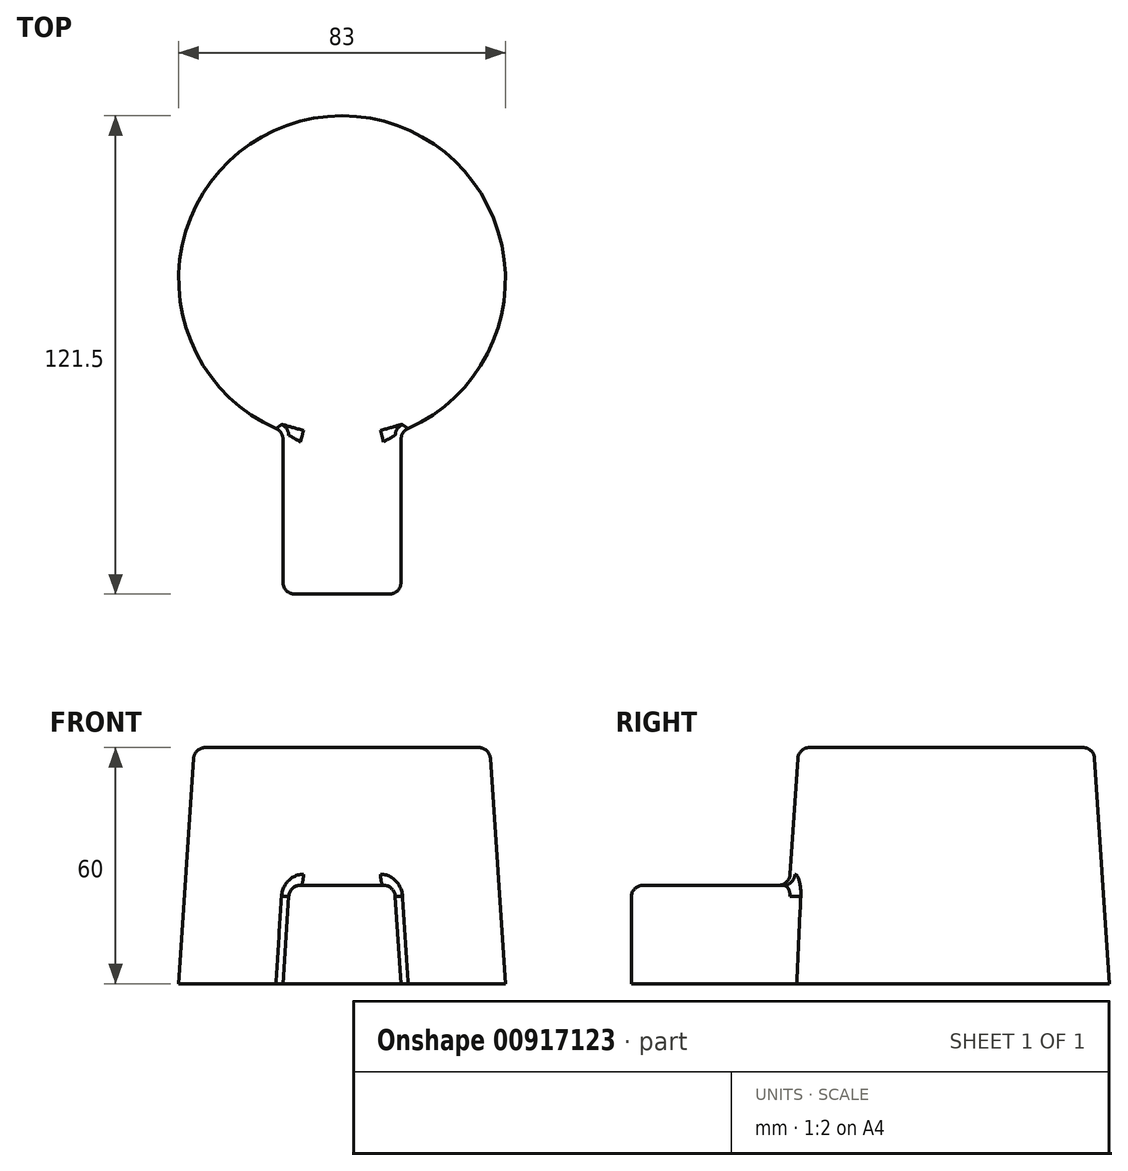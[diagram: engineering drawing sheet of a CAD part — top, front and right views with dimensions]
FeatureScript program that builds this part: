
annotation { "Feature Type Name" : "Feature", "Feature Type Description" : "" }
export const myFeature = defineFeature(function(context is Context, id is Id, definition is map)
    precondition{}
    {
        {
            var Q0;
            Q0=qCreatedBy(makeId("Top.planeOp"),FACE);
            var sketch = newSketch(context, id + "F0", { "sketchPlane" : qUnion([Q0])});
            skCircle(sketch, "E0", {"center": v(0, 0) * mm, "radius": 41.5 * mm});
            skSolve(sketch);
        }
        {
            var Q0;
            Q0 = qSketchRegion(id + "F0", true);
            extrude(context, id + "F1", {"entities" : qUnion([Q0]), "depth" : 60 * mm, "offsetDistance" : 25 * mm, "hasDraft" : true, "draftAngle" : 3.8 * degree, "draftPullDirection" : true});
        }
        {
            var Q0;
            Q0=qCreatedBy(makeId("Front.planeOp"),FACE);
            var sketch = newSketch(context, id + "F2", { "sketchPlane" : qUnion([Q0])});
            skLineSegment(sketch, "E1", {"start": v(-15, 0) * mm, "end": v(15, 0) * mm});
            skLineSegment(sketch, "E2", {"start": v(15, 0) * mm, "end": v(13.34, 25) * mm});
            skLineSegment(sketch, "E3", {"start": v(13.34, 25) * mm, "end": v(-13.34, 25) * mm});
            skLineSegment(sketch, "E4", {"start": v(-13.34, 25) * mm, "end": v(-15, 0) * mm});
            skLineSegment(sketch, "E5", {"start": v(0, 0) * mm, "end": v(0, 25) * mm, "construction": true});
            skSolve(sketch);
        }
        {
            var Q0;
            Q0 = qSketchRegion(id + "F2", true);
            extrude(context, id + "F3", {"entities" : qUnion([Q0]), "operationType" : NewBodyOperationType.ADD, "depth" : 80 * mm, "offsetDistance" : 25 * mm});
        }
        {
            var Q0;
            Q0=makeQuery(id+"F3.boolean.opBoolean","INTERSECT",EDGE,{"derivedFrom":[makeQuery(id+"F1.opExtrude","SWEPT_FACE",FACE,{"disambiguationData":[OSD([sQuery(id+"F0.wireOp",EDGE,"E0")])]}),makeQuery(id+"F3.opExtrude","SWEPT_FACE",FACE,{"disambiguationData":[OSD([sQuery(id+"F2.wireOp",EDGE,"E2")])]})]});
            var Q1;
            Q1=makeQuery(id+"F3.boolean.opBoolean","INTERSECT",EDGE,{"derivedFrom":[makeQuery(id+"F1.opExtrude","SWEPT_FACE",FACE,{"disambiguationData":[OSD([sQuery(id+"F0.wireOp",EDGE,"E0")])]}),makeQuery(id+"F3.opExtrude","SWEPT_FACE",FACE,{"disambiguationData":[OSD([sQuery(id+"F2.wireOp",EDGE,"E4")])]})]});
            var Q2;
            Q2=makeQuery(id+"F3.boolean.opBoolean","INTERSECT",EDGE,{"derivedFrom":[makeQuery(id+"F1.opExtrude","SWEPT_FACE",FACE,{"disambiguationData":[OSD([sQuery(id+"F0.wireOp",EDGE,"E0")])]}),makeQuery(id+"F3.opExtrude","SWEPT_FACE",FACE,{"disambiguationData":[OSD([sQuery(id+"F2.wireOp",EDGE,"E3")])]})]});
            var Q3;
            Q3=makeQuery(id+"F3.opExtrude","SWEPT_EDGE",EDGE,{"disambiguationData":[OSD([sQuery(id+"F2.wireOp",EDGE,"E3"),sQuery(id+"F2.wireOp",EDGE,"E4")])]});
            var Q4;
            Q4=makeQuery(id+"F3.opExtrude","CAP_EDGE",EDGE,{"disambiguationData":[OSD([sQuery(id+"F2.wireOp",EDGE,"E4")])],"isStart":false});
            var Q5;
            Q5=makeQuery(id+"F3.opExtrude","CAP_EDGE",EDGE,{"disambiguationData":[OSD([sQuery(id+"F2.wireOp",EDGE,"E2")])],"isStart":false});
            var Q6;
            Q6=makeQuery(id+"F3.opExtrude","CAP_EDGE",EDGE,{"disambiguationData":[OSD([sQuery(id+"F2.wireOp",EDGE,"E3")])],"isStart":false});
            var Q7;
            Q7=makeQuery(id+"F3.opExtrude","SWEPT_EDGE",EDGE,{"disambiguationData":[OSD([sQuery(id+"F2.wireOp",EDGE,"E2"),sQuery(id+"F2.wireOp",EDGE,"E3")])]});
            var Q8;
            Q8=makeQuery(id+"F1.opExtrude","CAP_EDGE",EDGE,{"disambiguationData":[OSD([sQuery(id+"F0.wireOp",EDGE,"E0")])],"isStart":false});
            fillet(context, id + "F4", {"entities" : qUnion([Q0, Q1, Q2, Q3, Q4, Q5, Q6, Q7, Q8]), "radius" : 3 * mm, "tangentPropagation" : true, "allowEdgeOverflow" : false});
        }
    });
